# Revit family: EKF_EE_ЦокольЩРМ_PROxima
name_source: partatom
category: Электрооборудование
units: mm (PartAtom-declared; Revit-internal decimal feet)

## family parameters
Всегда вертикально = Нет
На основе рабочей плоскости = Да
Общий = Да
При загрузке вырезать с полостями = Нет
Размер круглого соединителя = Использовать диаметр
Тип детали = Силовой щит
Точка расчета площади = Нет

## types (2) — shared parameters
ADSK_Единица измерения = шт.
ADSK_Завод-изготовитель = EKF
ADSK_Количество = 1
ADSK_Марка = Цоколь
ADSK_Материал = RAL 7035_Сталь
ADSK_Обозначение = Цоколь
ADSK_Размер_Высота = 100 мм
ADSK_Размер_Глубина = 400 мм
l1 = 197 мм
Изготовитель = EKF
Серия номенклатуры = PROxima
Степень защиты IP = -
ТВ = EKF_2
Тип установки = -
ШиринаОтступа = 101.5 мм
zero-valued in all types: ADSK_Масса, Отметка по умолчанию

## per-type parameters (varying)
| type | ADSK_Код изделия | ADSK_Наименование | ADSK_Размер_Ширина | l2 | Тип |
| Цоколь 100х600х400мм (ЩРНМ-8, ЩРНМ-9) | c-100x600 | Цоколь 100х600х400мм (ЩРНМ-8 ЩРНМ-9) | 600 мм | 397 мм | 144 мм |
| Цоколь 100х800х400мм (ЩРНМ-8L, ЩРНМ-9L) | c-100x800 | Цоколь 100х800х400мм (ЩРНМ-8L ЩРНМ-9L) | 800 мм | 597 мм | 145 мм |
